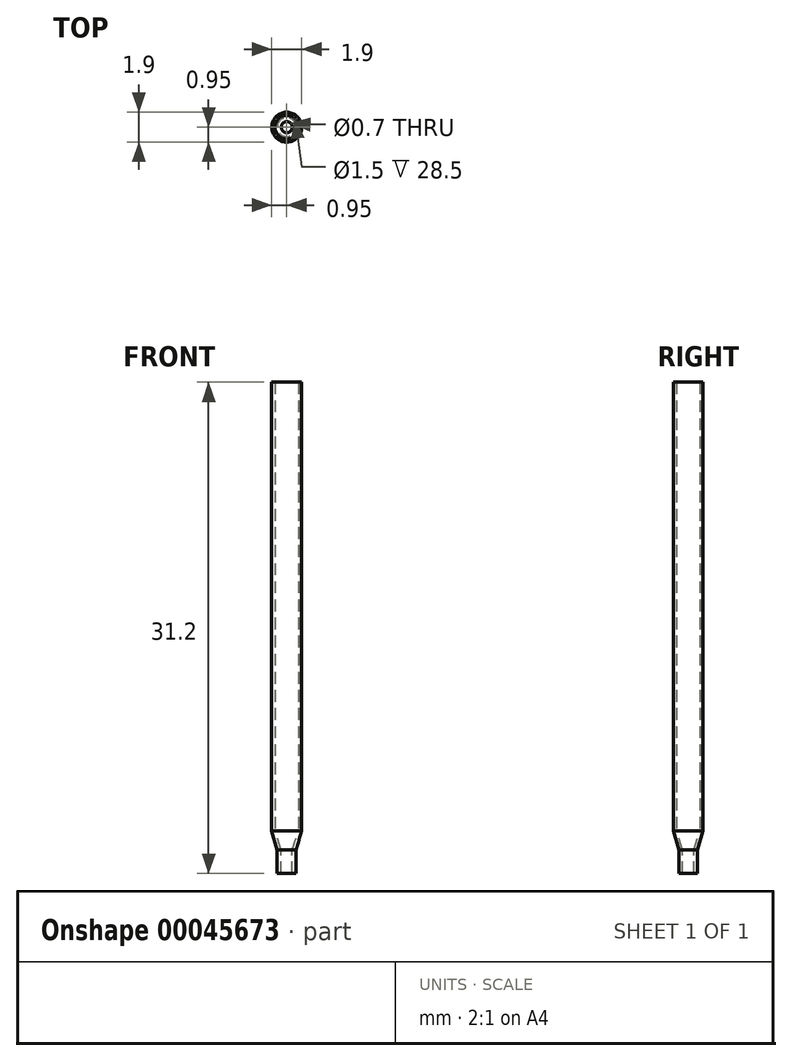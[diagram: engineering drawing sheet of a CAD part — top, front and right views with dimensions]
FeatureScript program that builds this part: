
annotation { "Feature Type Name" : "Feature", "Feature Type Description" : "" }
export const myFeature = defineFeature(function(context is Context, id is Id, definition is map)
    precondition{}
    {
        {
            var Q0;
            Q0=qCreatedBy(makeId("Top.planeOp"),FACE);
            var sketch = newSketch(context, id + "F0", { "sketchPlane" : qUnion([Q0])});
            skCircle(sketch, "E0", {"center": v(0, 0) * mm, "radius": 0.6 * mm});
            skSolve(sketch);
        }
        {
            var Q0;
            Q0=makeQuery(id+"F0.imprint","IMPRINT",FACE,{"disambiguationData":[TD([[makeQuery(id+"F0.imprint","IMPRINT",EDGE,{"derivedFrom":sQuery(id+"F0.wireOp",EDGE,"E0")}),1.0]])]});
            cPlane(context, id + "F1", {"entities" : qUnion([Q0]), "cplaneType" : CPlaneType.OFFSET, "offset" : 1.2 * mm, "width" : 150 * mm, "height" : 150 * mm});
        }
        {
            var Q0;
            Q0=qCreatedBy(id+"F1.planeOp",FACE);
            var sketch = newSketch(context, id + "F2", { "sketchPlane" : qUnion([Q0])});
            skCircle(sketch, "E1", {"center": v(0, 0) * mm, "radius": 0.95 * mm});
            skSolve(sketch);
        }
        {
            var Q0;
            Q0=qSketchRegion(id+"F0",true);
            var Q1;
            Q1=qSketchRegion(id+"F2",true);
            loft(context, id + "F3", {"sheetProfilesArray" : [{ "sheetProfileEntities" : qUnion([Q0]) }, { "sheetProfileEntities" : qUnion([Q1]) }]});
        }
        {
            var Q0;
            Q0=makeQuery(id+"F3.opLoft","CAP_FACE",FACE,{"disambiguationData":[OSD([makeQuery(id+"F0.imprint","IMPRINT",FACE,{"disambiguationData":[TD([[makeQuery(id+"F0.imprint","IMPRINT",EDGE,{"derivedFrom":sQuery(id+"F0.wireOp",EDGE,"E0")}),1.0]])]})])],"isStart":true});
            var sketch = newSketch(context, id + "F4", { "sketchPlane" : qUnion([Q0])});
            skCircle(sketch, "E2", {"center": v(0, 0) * mm, "radius": 0.35 * mm});
            skSolve(sketch);
        }
        {
            var Q0;
            Q0=makeQuery(id+"F3.opLoft","CAP_FACE",FACE,{"disambiguationData":[OSD([makeQuery(id+"F2.imprint","IMPRINT",FACE,{"disambiguationData":[TD([[makeQuery(id+"F2.imprint","IMPRINT",EDGE,{"derivedFrom":sQuery(id+"F2.wireOp",EDGE,"E1")}),1.0]])]})])],"isStart":true});
            var sketch = newSketch(context, id + "F5", { "sketchPlane" : qUnion([Q0])});
            skCircle(sketch, "E3", {"center": v(0, 0) * mm, "radius": 0.75 * mm});
            skSolve(sketch);
        }
        {
            var Q1;
            Q1=qSketchRegion(id+"F5",true);
            var Q2;
            Q2=qSketchRegion(id+"F4",true);
            loft(context, id + "F6", {"operationType" : NewBodyOperationType.REMOVE, "sheetProfilesArray" : [{ "sheetProfileEntities" : qUnion([Q1]) }, { "sheetProfileEntities" : qUnion([Q2]) }]});
        }
        {
            var Q0;
            Q0=makeQuery(id+"F3.opLoft","CAP_FACE",FACE,{"disambiguationData":[OSD([makeQuery(id+"F0.imprint","IMPRINT",FACE,{"disambiguationData":[TD([[makeQuery(id+"F0.imprint","IMPRINT",EDGE,{"derivedFrom":sQuery(id+"F0.wireOp",EDGE,"E0")}),1.0]])]})])],"isStart":true});
            extrude(context, id + "F7", {"entities" : qUnion([Q0]), "operationType" : NewBodyOperationType.ADD, "depth" : 1.5 * mm});
        }
        {
            var Q0;
            Q0=makeQuery(id+"F3.opLoft","CAP_FACE",FACE,{"disambiguationData":[OSD([makeQuery(id+"F2.imprint","IMPRINT",FACE,{"disambiguationData":[TD([[makeQuery(id+"F2.imprint","IMPRINT",EDGE,{"derivedFrom":sQuery(id+"F2.wireOp",EDGE,"E1")}),1.0]])]})])],"isStart":true});
            extrude(context, id + "F8", {"entities" : qUnion([Q0]), "operationType" : NewBodyOperationType.ADD, "depth" : 28.5 * mm});
        }
    });
